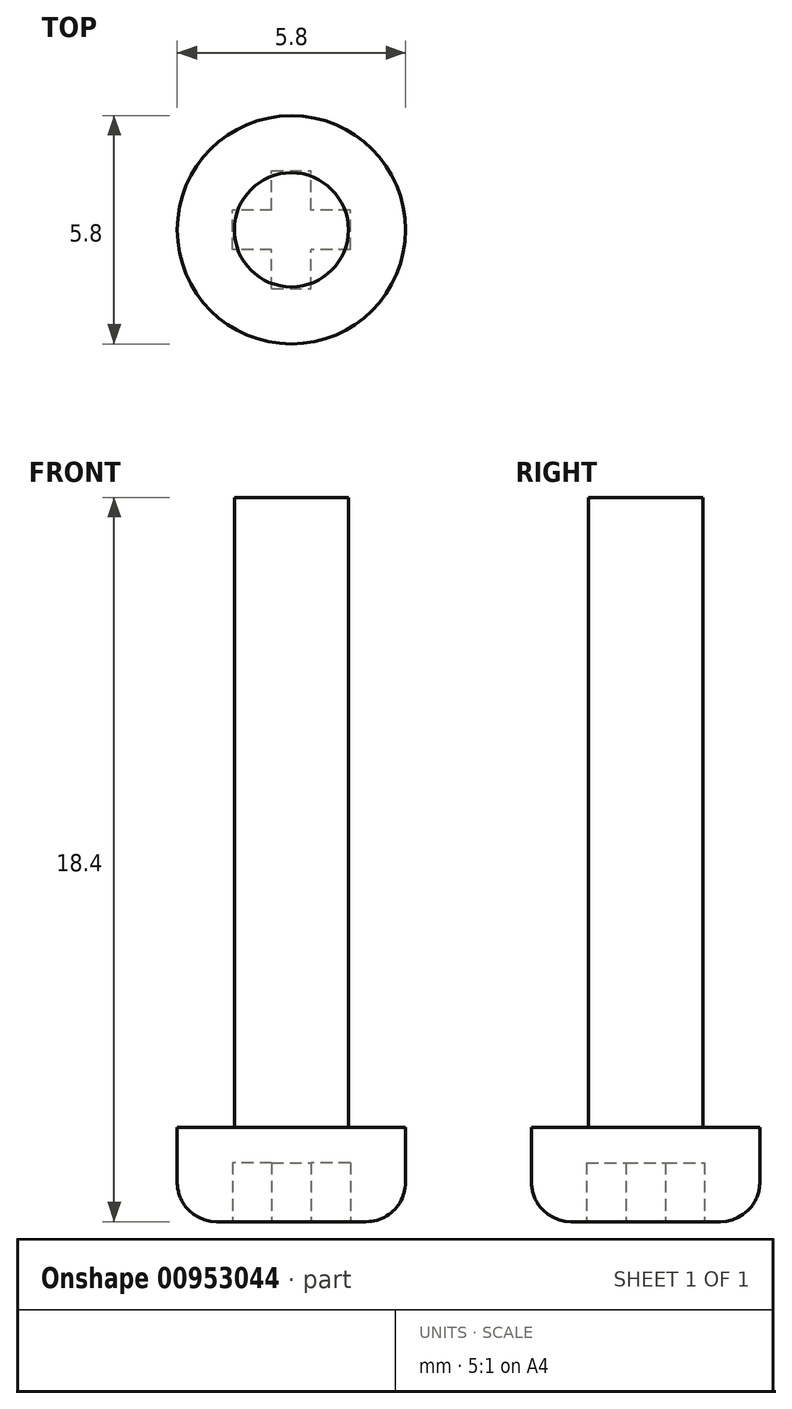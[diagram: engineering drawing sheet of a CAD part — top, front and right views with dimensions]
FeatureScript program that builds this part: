
annotation { "Feature Type Name" : "Feature", "Feature Type Description" : "" }
export const myFeature = defineFeature(function(context is Context, id is Id, definition is map)
    precondition{}
    {
        {
            var Q0;
            Q0=qCreatedBy(makeId("Top.planeOp"),FACE);
            var sketch = newSketch(context, id + "F0", { "sketchPlane" : qUnion([Q0])});
            skCircle(sketch, "E0", {"center": v(0, 0) * mm, "radius": 1.45 * mm});
            skSolve(sketch);
        }
        {
            var Q0;
            Q0=qSketchRegion(id+"F0",true);
            extrude(context, id + "F1", {"entities" : qUnion([Q0]), "offsetDistance" : 25 * mm, "depth" : 16 * mm});
        }
        {
            var Q0;
            Q0=qCreatedBy(makeId("Top.planeOp"),FACE);
            var sketch = newSketch(context, id + "F2", { "sketchPlane" : qUnion([Q0])});
            skCircle(sketch, "E1", {"center": v(0, 0) * mm, "radius": 2.9 * mm});
            skSolve(sketch);
        }
        {
            var Q0;
            Q0=qSketchRegion(id+"F2",true);
            extrude(context, id + "F3", {"entities" : qUnion([Q0]), "operationType" : NewBodyOperationType.ADD, "oppositeDirection" : true, "depth" : 2.4 * mm});
        }
        {
            var Q0;
            Q0=makeQuery(id+"F3.opExtrude","CAP_EDGE",EDGE,{"disambiguationData":[OSD([sQuery(id+"F2.wireOp",EDGE,"E1")])],"isStart":false});
            fillet(context, id + "F4", {"entities" : qUnion([Q0]), "radius" : 1 * mm, "tangentPropagation" : true, "allowEdgeOverflow" : false});
        }
        {
            var Q0;
            Q0=makeQuery(id+"F3.opExtrude","CAP_FACE",FACE,{"disambiguationData":[OSD([sQuery(id+"F2.wireOp",EDGE,"E1")])],"isStart":false});
            var sketch = newSketch(context, id + "F5", { "sketchPlane" : qUnion([Q0])});
            skLineSegment(sketch, "E2.bottom", {"start": v(1.5, 0.5) * mm, "end": v(-1.5, 0.5) * mm});
            skLineSegment(sketch, "E2.top", {"start": v(1.5, -0.5) * mm, "end": v(-1.5, -0.5) * mm});
            skLineSegment(sketch, "E2.left", {"start": v(1.5, 0.5) * mm, "end": v(1.5, -0.5) * mm});
            skLineSegment(sketch, "E2.right", {"start": v(-1.5, 0.5) * mm, "end": v(-1.5, -0.5) * mm});
            skPoint(sketch, "E2.middle", {"position": v(0, 0) * mm});
            skLineSegment(sketch, "E3.bottom", {"start": v(-0.5, 1.5) * mm, "end": v(0.5, 1.5) * mm});
            skLineSegment(sketch, "E3.top", {"start": v(-0.5, -1.5) * mm, "end": v(0.5, -1.5) * mm});
            skLineSegment(sketch, "E3.left", {"start": v(-0.5, 1.5) * mm, "end": v(-0.5, -1.5) * mm});
            skLineSegment(sketch, "E3.right", {"start": v(0.5, 1.5) * mm, "end": v(0.5, -1.5) * mm});
            skSolve(sketch);
        }
        {
            var Q0;
            Q0=qSketchRegion(id+"F5",true);
            extrude(context, id + "F6", {"entities" : qUnion([Q0]), "operationType" : NewBodyOperationType.REMOVE, "oppositeDirection" : true, "depth" : 1.5 * mm});
        }
    });
